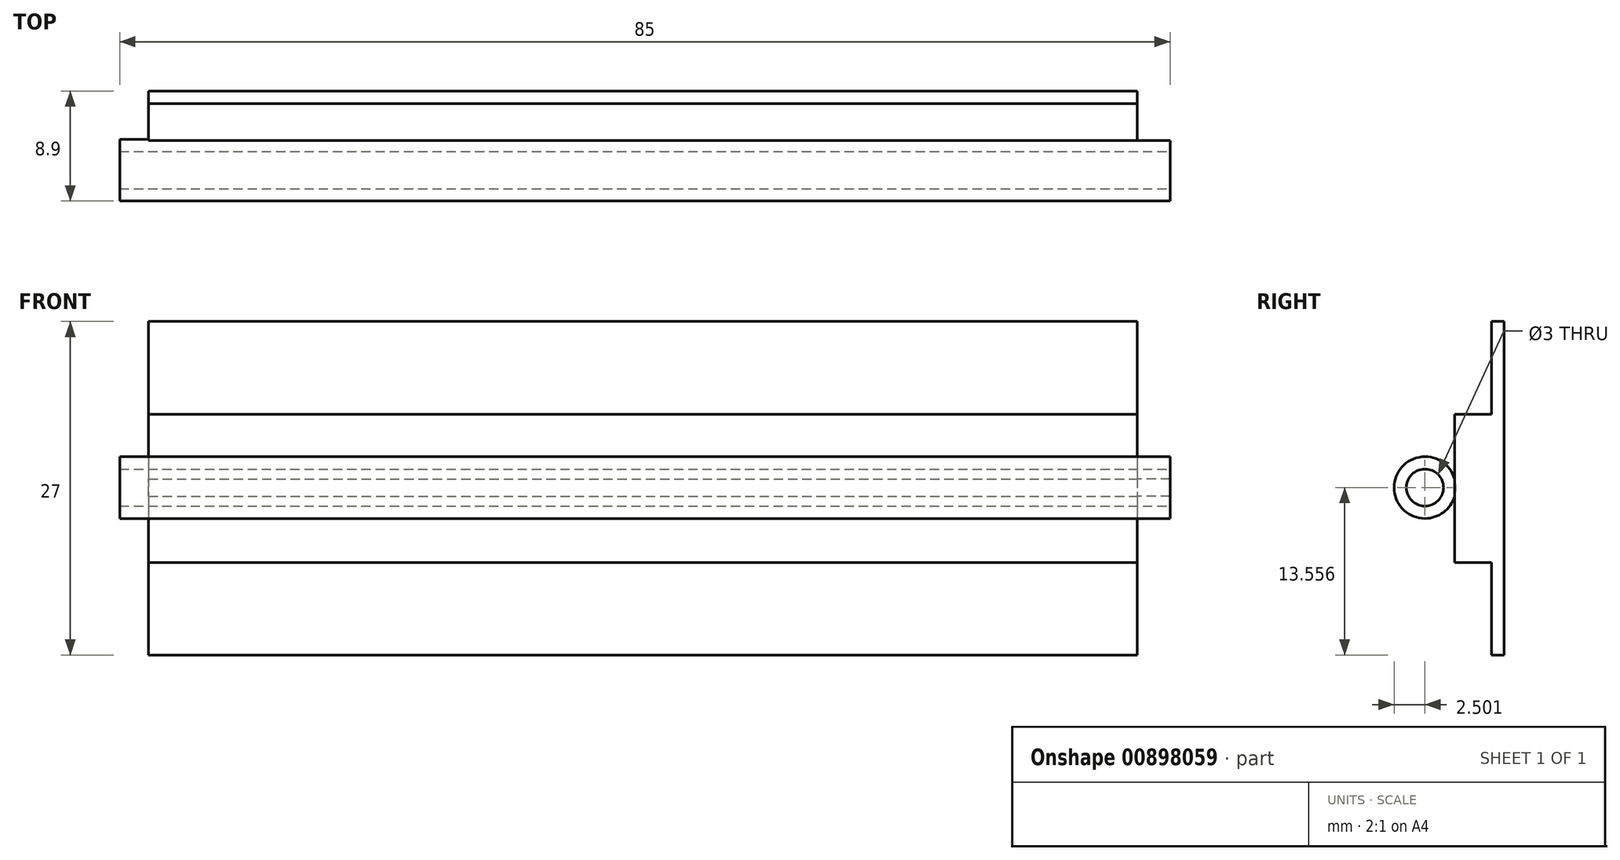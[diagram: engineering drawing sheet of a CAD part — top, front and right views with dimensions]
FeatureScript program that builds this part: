
annotation { "Feature Type Name" : "Feature", "Feature Type Description" : "" }
export const myFeature = defineFeature(function(context is Context, id is Id, definition is map)
    precondition{}
    {
        {
            var Q0;
            Q0=qCreatedBy(makeId("Front.planeOp"),FACE);
            var sketch = newSketch(context, id + "F0", { "sketchPlane" : qUnion([Q0])});
            skLineSegment(sketch, "E0.bottom", {"start": v(-47.67, 27) * mm, "end": v(32.33, 27) * mm});
            skLineSegment(sketch, "E0.top", {"start": v(-47.67, 0) * mm, "end": v(32.33, 0) * mm});
            skLineSegment(sketch, "E0.left", {"start": v(-47.67, 27) * mm, "end": v(-47.67, 0) * mm});
            skLineSegment(sketch, "E0.right", {"start": v(32.33, 27) * mm, "end": v(32.33, 0) * mm});
            skLineSegment(sketch, "E1", {"start": v(-47.67, 13.5) * mm, "end": v(-47.67, 7.5) * mm});
            skLineSegment(sketch, "E2", {"start": v(-47.67, 7.5) * mm, "end": v(32.33, 7.5) * mm});
            skLineSegment(sketch, "E3", {"start": v(32.33, 7.5) * mm, "end": v(32.33, 13.5) * mm});
            skLineSegment(sketch, "E4", {"start": v(32.33, 13.5) * mm, "end": v(-47.67, 13.5) * mm});
            skLineSegment(sketch, "E5", {"start": v(-47.67, 13.5) * mm, "end": v(-47.67, 19.5) * mm});
            skLineSegment(sketch, "E6", {"start": v(-47.67, 19.5) * mm, "end": v(32.33, 19.5) * mm});
            skLineSegment(sketch, "E7", {"start": v(32.33, 19.5) * mm, "end": v(32.33, 13.5) * mm});
            skSolve(sketch);
        }
        {
            var Q0;
            {var subQ0=sQuery(id+"F0.wireOp",EDGE,"E4");Q0=makeQuery(id+"F0.imprint","IMPRINT",FACE,{"disambiguationData":[TD([[makeQuery(id+"F0.imprint","IMPRINT",EDGE,{"derivedFrom":subQ0}),-1.0]])]});}
            var Q1;
            {var subQ2=sQuery(id+"F0.wireOp",EDGE,"E2");Q1=makeQuery(id+"F0.imprint","IMPRINT",FACE,{"disambiguationData":[TD([[makeQuery(id+"F0.imprint","IMPRINT",EDGE,{"derivedFrom":subQ2}),1.0]])]});}
            extrude(context, id + "F1", {"entities" : qUnion([Q0, Q1]), "depth" : 3 * mm, "offsetDistance" : 25 * mm});
        }
        {
            var Q0;
            {var subQ0=sQuery(id+"F0.wireOp",EDGE,"E4");var subQ8=makeQuery(id+"F0.imprint","IMPRINT",EDGE,{"derivedFrom":subQ0});var subQ10=sQuery(id+"F0.wireOp",EDGE,"E2");var subQ13=makeQuery(id+"F0.imprint","IMPRINT",EDGE,{"derivedFrom":subQ10});var subQ14=sQuery(id+"F0.wireOp",EDGE,"E0.top");var subQ15=sQuery(id+"F0.wireOp",EDGE,"E0.bottom");Q0=qUnion([makeQuery(id+"F0.imprint","IMPRINT",FACE,{"disambiguationData":[TD([[makeQuery(id+"F0.imprint","IMPRINT",EDGE,{"derivedFrom":subQ15}),-1.0]])]}),makeQuery(id+"F0.imprint","IMPRINT",FACE,{"disambiguationData":[TD([[makeQuery(id+"F0.imprint","IMPRINT",EDGE,{"derivedFrom":subQ14}),1.0]])]}),makeQuery(id+"F0.imprint","IMPRINT",FACE,{"disambiguationData":[TD([[subQ13,1.0]])]}),makeQuery(id+"F0.imprint","IMPRINT",FACE,{"disambiguationData":[TD([[subQ8,-1.0]])]})]);}
            extrude(context, id + "F2", {"entities" : qUnion([Q0]), "operationType" : NewBodyOperationType.ADD, "oppositeDirection" : true, "depth" : 1 * mm, "offsetDistance" : 25 * mm});
        }
        {
            var Q0;
            Q0=qCreatedBy(makeId("Right.planeOp"),FACE);
            var sketch = newSketch(context, id + "F3", { "sketchPlane" : qUnion([Q0])});
            skCircle(sketch, "E8", {"center": v(-5.4, 13.56) * mm, "radius": 2.5 * mm});
            skCircle(sketch, "E9", {"center": v(-5.4, 13.56) * mm, "radius": 1.5 * mm});
            skSolve(sketch);
        }
        {
            var Q0;
            Q0=makeQuery(id+"F3.imprint","IMPRINT",FACE,{"disambiguationData":[TD([[makeQuery(id+"F3.imprint","IMPRINT",EDGE,{"derivedFrom":sQuery(id+"F3.wireOp",EDGE,"E8")}),1.0]])]});
            extrude(context, id + "F4", {"entities" : qUnion([Q0]), "operationType" : NewBodyOperationType.ADD, "oppositeDirection" : true, "depth" : 50 * mm, "offsetDistance" : 25 * mm});
        }
        {
            var Q0;
            Q0=makeQuery(id+"F4.opExtrude","CAP_FACE",FACE,{"disambiguationData":[OSD([sQuery(id+"F3.wireOp",EDGE,"E8"),sQuery(id+"F3.wireOp",EDGE,"E9")])],"isStart":true});
            extrude(context, id + "F5", {"entities" : qUnion([Q0]), "operationType" : NewBodyOperationType.ADD, "depth" : 35 * mm, "offsetDistance" : 25 * mm});
        }
    });
